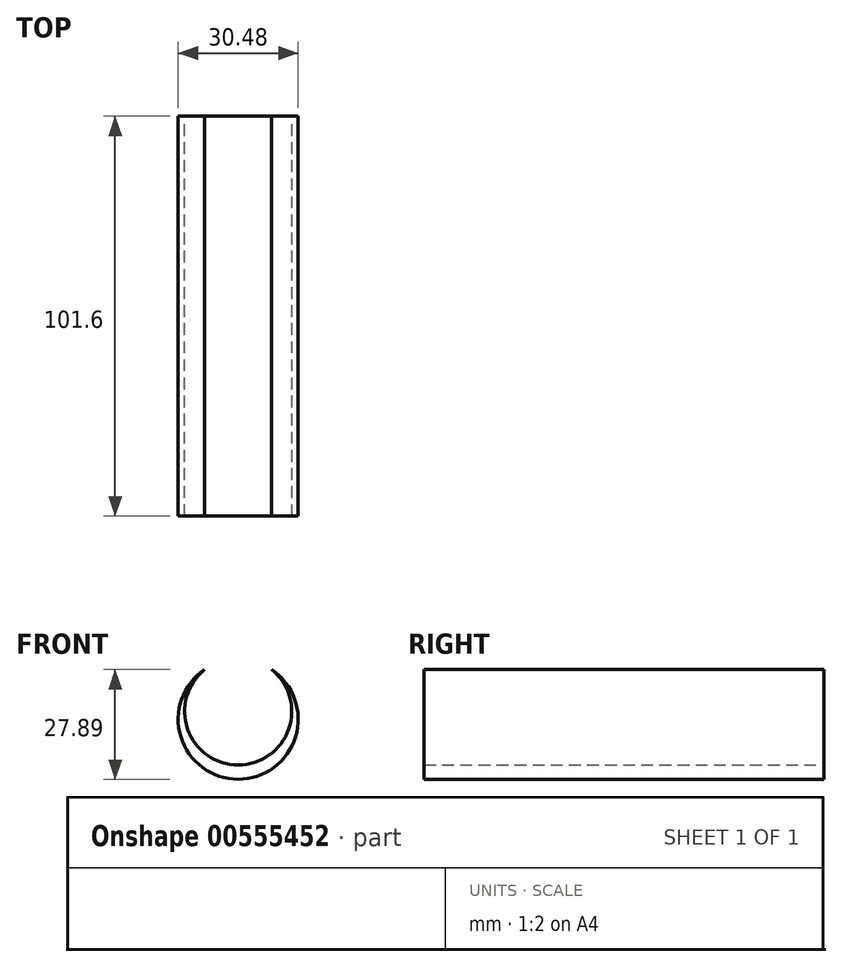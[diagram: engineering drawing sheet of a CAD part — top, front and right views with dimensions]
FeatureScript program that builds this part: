
annotation { "Feature Type Name" : "Feature", "Feature Type Description" : "" }
export const myFeature = defineFeature(function(context is Context, id is Id, definition is map)
    precondition{}
    {
        {
            var Q0;
            Q0=qCreatedBy(makeId("Front.planeOp"),FACE);
            var sketch = newSketch(context, id + "F0", { "sketchPlane" : qUnion([Q0])});
            skPoint(sketch, "E0.center.orphan", {"position": v(-43.73, 0) * mm});
            skArc(sketch, "E1", {"start": v(-60.72, 0) * mm, "mid": v(-52.23, -27.9) * mm, "end": v(-43.73, 0) * mm});
            skArc(sketch, "E2", {"start": v(-60.72, 0) * mm, "mid": v(-52.23, -24.25) * mm, "end": v(-43.73, 0) * mm});
            skSolve(sketch);
        }
        {
            var Q0;
            Q0=qSketchRegion(id+"F0",true);
            extrude(context, id + "F1", {"entities" : qUnion([Q0]), "depth" : 101.6 * mm, "offsetDistance" : 25.4 * mm});
        }
    });
